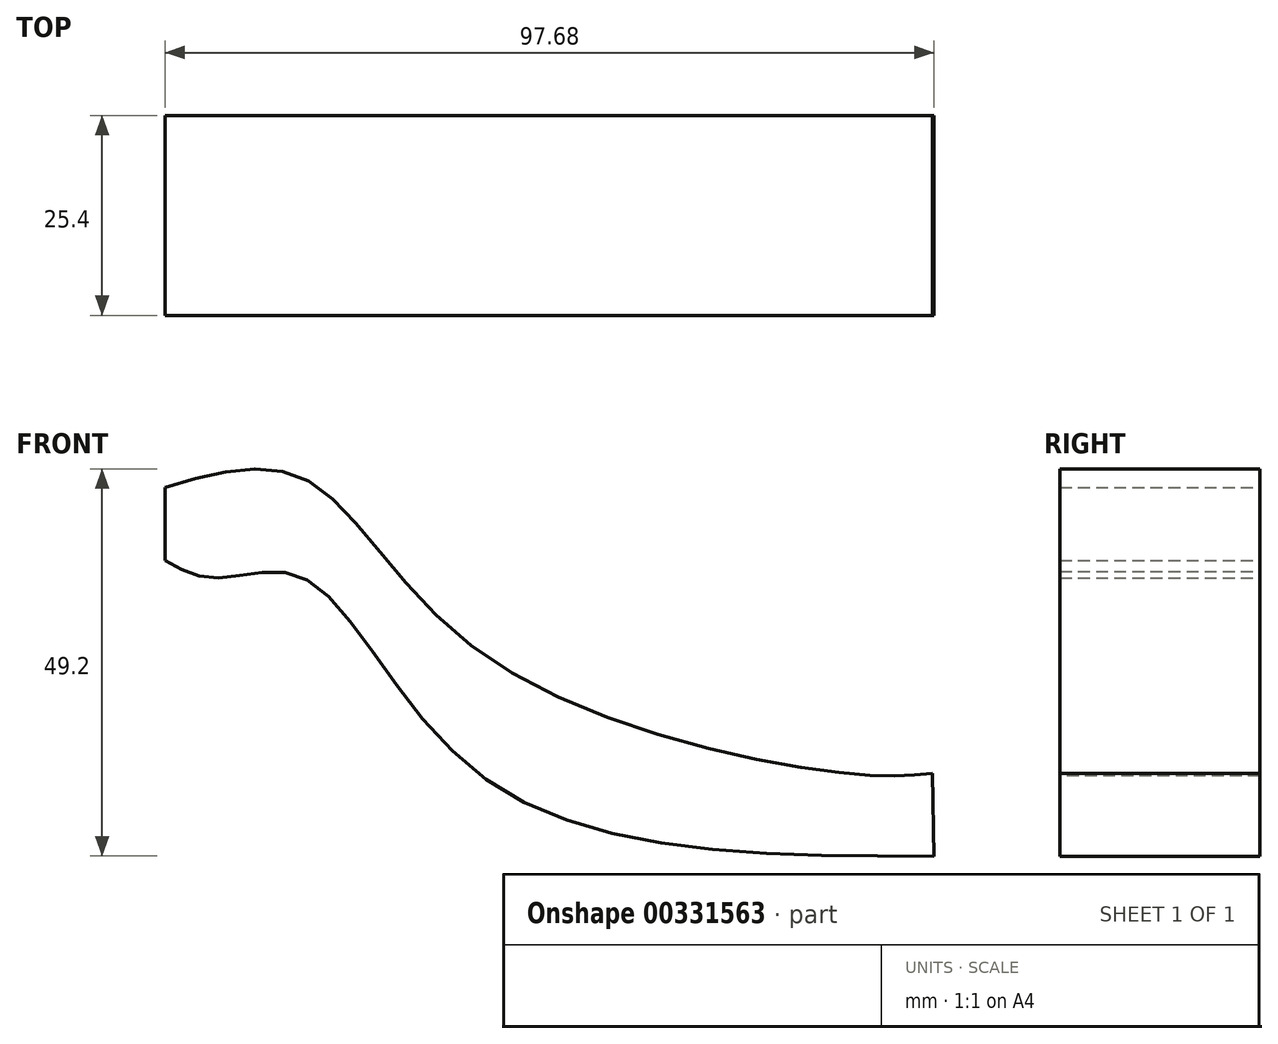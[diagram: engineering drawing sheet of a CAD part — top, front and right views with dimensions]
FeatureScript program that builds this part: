
annotation { "Feature Type Name" : "Feature", "Feature Type Description" : "" }
export const myFeature = defineFeature(function(context is Context, id is Id, definition is map)
    precondition{}
    {
        {
            var Q0;
            Q0=qCreatedBy(makeId("Front.planeOp"),FACE);
            var sketch = newSketch(context, id + "F0", { "sketchPlane" : qUnion([Q0])});
            skFitSpline(sketch, "E0", {"points": [v(-52.78, 36.35) * mm, v(-35.2, 37.47) * mm, v(-13.05, 15.58) * mm, v(33.7, 0) * mm, v(44.73, 0) * mm], "startDerivative": vector(89.6, 25.9) * mm, "endDerivative": vector(51.83, 4.88) * mm});
            skLineSegment(sketch, "E1", {"start": v(-52.78, 36.35) * mm, "end": v(-52.78, 24.85) * mm});
            skFitSpline(sketch, "E2", {"points": [v(-54.13, 27.88) * mm, v(-46.55, 24.85) * mm, v(-35.2, 24.85) * mm, v(-13.05, 0) * mm, v(44.9, -10.51) * mm], "startDerivative": vector(48.5, -30.58) * mm, "endDerivative": vector(170.41, 0.03) * mm});
            skLineSegment(sketch, "E3", {"start": v(44.73, 0) * mm, "end": v(44.9, -10.51) * mm});
            skSolve(sketch);
        }
        {
            var Q0;
            Q0 = qSketchRegion(id + "F0", true);
            extrude(context, id + "F1", {"entities" : qUnion([Q0]), "depth" : 25.4 * mm});
        }
    });
